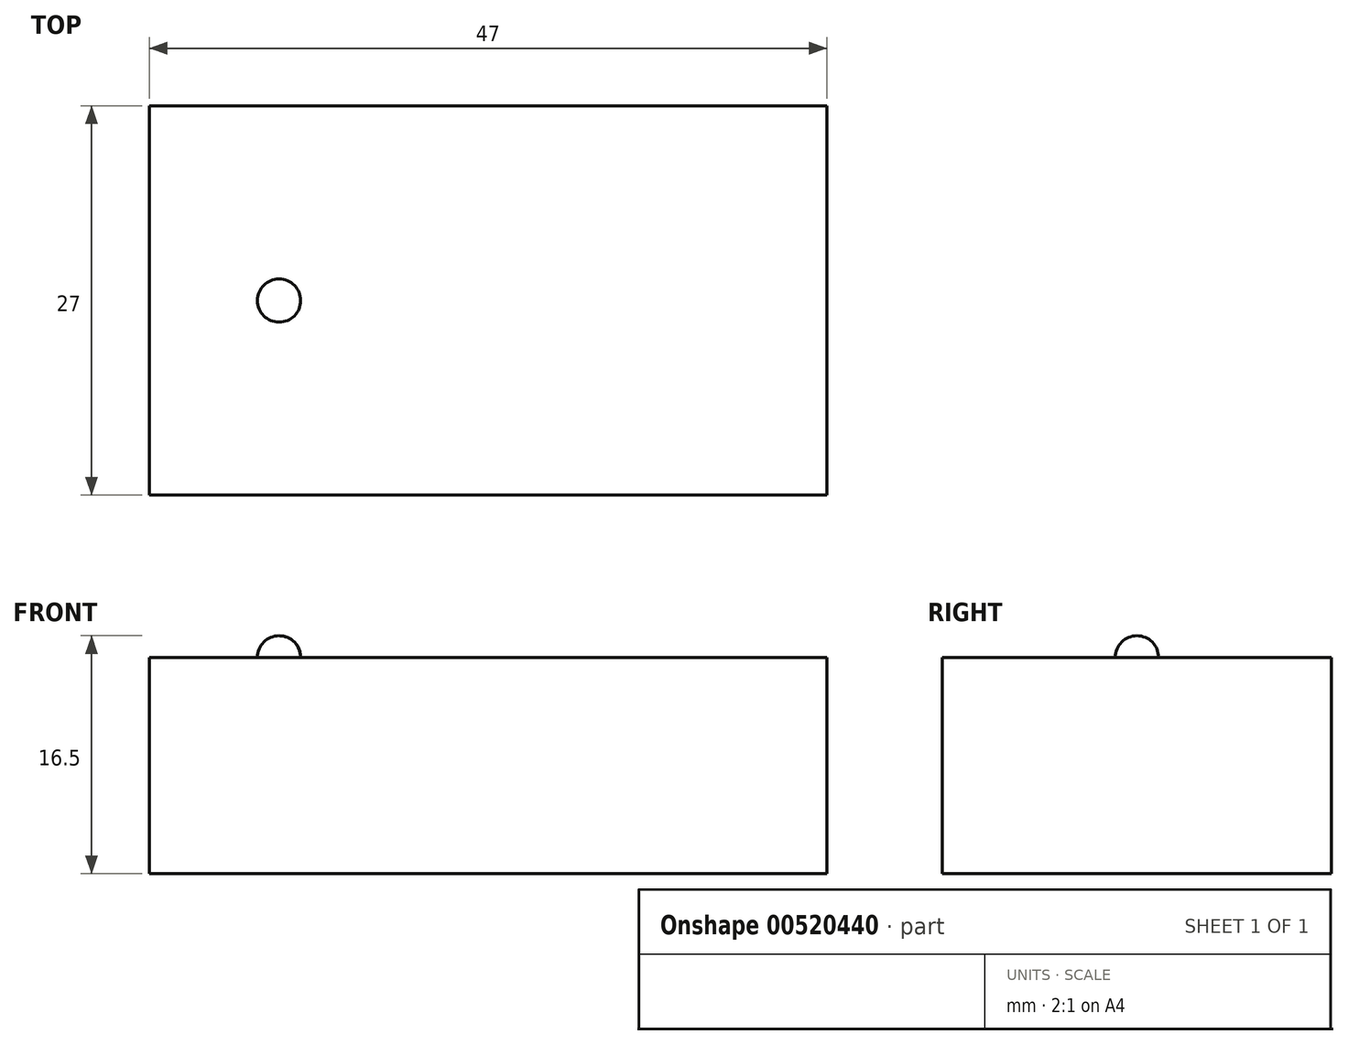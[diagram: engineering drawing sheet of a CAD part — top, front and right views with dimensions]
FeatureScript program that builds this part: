
annotation { "Feature Type Name" : "Feature", "Feature Type Description" : "" }
export const myFeature = defineFeature(function(context is Context, id is Id, definition is map)
    precondition{}
    {
        {
            var Q0;
            Q0=qCreatedBy(makeId("Front.planeOp"),FACE);
            var sketch = newSketch(context, id + "F0", { "sketchPlane" : qUnion([Q0])});
            skLineSegment(sketch, "E0.bottom", {"start": v(0, 15) * mm, "end": v(47, 15) * mm});
            skLineSegment(sketch, "E0.top", {"start": v(0, 0) * mm, "end": v(47, 0) * mm});
            skLineSegment(sketch, "E0.left", {"start": v(0, 15) * mm, "end": v(0, 0) * mm});
            skLineSegment(sketch, "E0.right", {"start": v(47, 15) * mm, "end": v(47, 0) * mm});
            skSolve(sketch);
        }
        {
            var Q0;
            Q0 = qSketchRegion(id + "F0", true);
            extrude(context, id + "F1", {"entities" : qUnion([Q0]), "depth" : 27 * mm, "offsetDistance" : 25 * mm});
        }
        {
            var Q0;
            Q0=makeQuery(id+"F1.opExtrude","SWEPT_FACE",FACE,{"disambiguationData":[OSD([sQuery(id+"F0.wireOp",EDGE,"E0.bottom")])]});
            var sketch = newSketch(context, id + "F2", { "sketchPlane" : qUnion([Q0])});
            skCircle(sketch, "E1", {"center": v(9, -13.5) * mm, "radius": 1.5 * mm});
            skLineSegment(sketch, "E2", {"start": v(0, -13.5) * mm, "end": v(47, -13.5) * mm, "construction": true});
            skSolve(sketch);
        }
        {
            var Q0;
            Q0=makeQuery(id+"F2.imprint","IMPRINT",FACE,{"disambiguationData":[TD([[makeQuery(id+"F2.imprint","IMPRINT",EDGE,{"derivedFrom":sQuery(id+"F2.wireOp",EDGE,"E1")}),1.0]])]});
            var Q1;
            Q1=sQuery(id+"F2.wireOp",EDGE,"E1");
            extrude(context, id + "F3", {"entities" : qUnion([Q0]), "surfaceEntities" : qUnion([Q1]), "depth" : 1.5 * mm, "offsetDistance" : 25 * mm});
        }
        {
            var Q0;
            Q0=makeQuery(id+"F3.opExtrude","CAP_EDGE",EDGE,{"disambiguationData":[OSD([sQuery(id+"F2.wireOp",EDGE,"E1")])],"isStart":false});
            fillet(context, id + "F4", {"entities" : qUnion([Q0]), "radius" : 1.5 * mm, "tangentPropagation" : true, "allowEdgeOverflow" : false});
        }
    });
